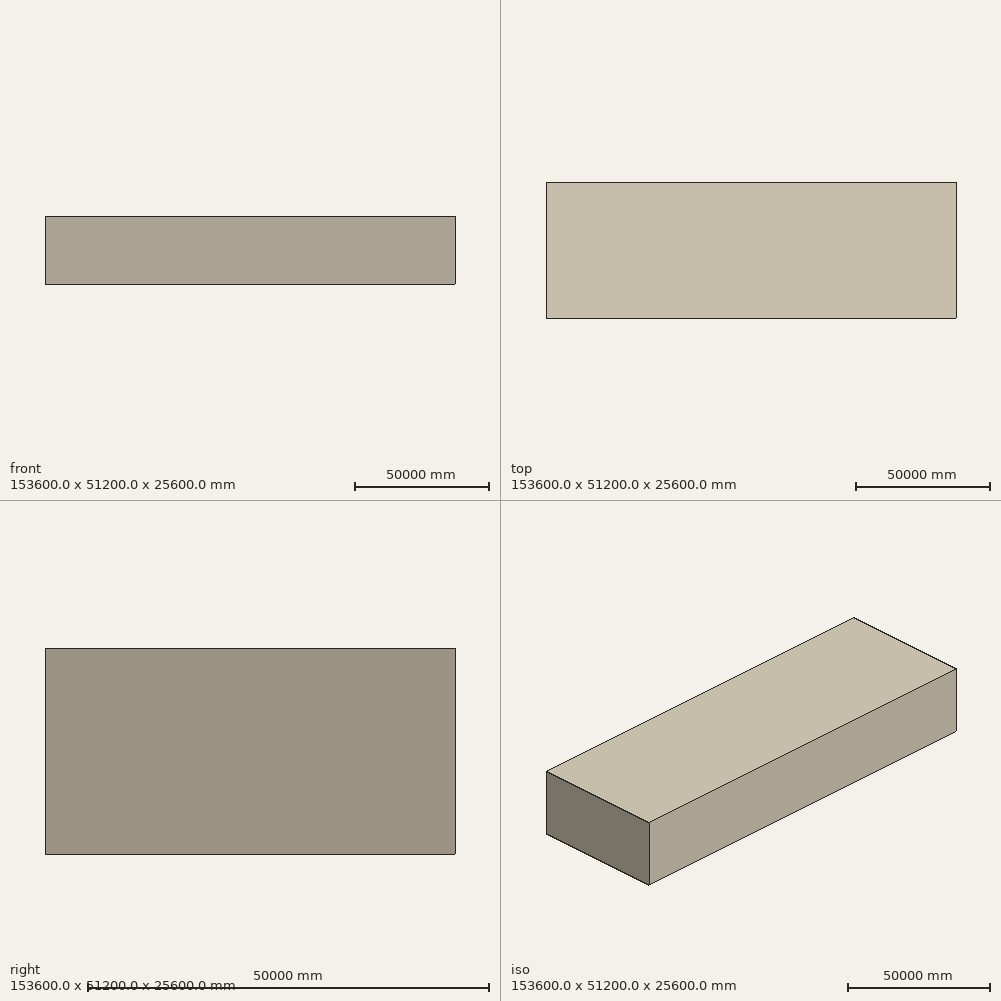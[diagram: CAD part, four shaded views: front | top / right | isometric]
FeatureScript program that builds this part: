
annotation { "Feature Type Name" : "Feature", "Feature Type Description" : "" }
export const myFeature = defineFeature(function(context is Context, id is Id, definition is map)
    precondition{}
    {
        {
            var Q0;
            Q0=qCreatedBy(makeId("Front.planeOp"),FACE);
            var sketch = newSketch(context, id + "F0", { "sketchPlane" : qUnion([Q0])});
            skLineSegment(sketch, "E0.bottom", {"start": v(-51000, 25600) * mm, "end": v(102600, 25600) * mm});
            skLineSegment(sketch, "E0.top", {"start": v(-51000, 0) * mm, "end": v(102600, 0) * mm});
            skLineSegment(sketch, "E0.left", {"start": v(-51000, 25600) * mm, "end": v(-51000, 0) * mm});
            skLineSegment(sketch, "E0.right", {"start": v(102600, 25600) * mm, "end": v(102600, 0) * mm});
            skSolve(sketch);
        }
        {
            var Q0;
            Q0=qSketchRegion(id+"F0",true);
            extrude(context, id + "F1", {"entities" : qUnion([Q0]), "depth" : 25600 * mm, "hasSecondDirection" : true, "secondDirectionOppositeDirection" : true, "secondDirectionDepth" : 25600 * mm});
        }
    });
